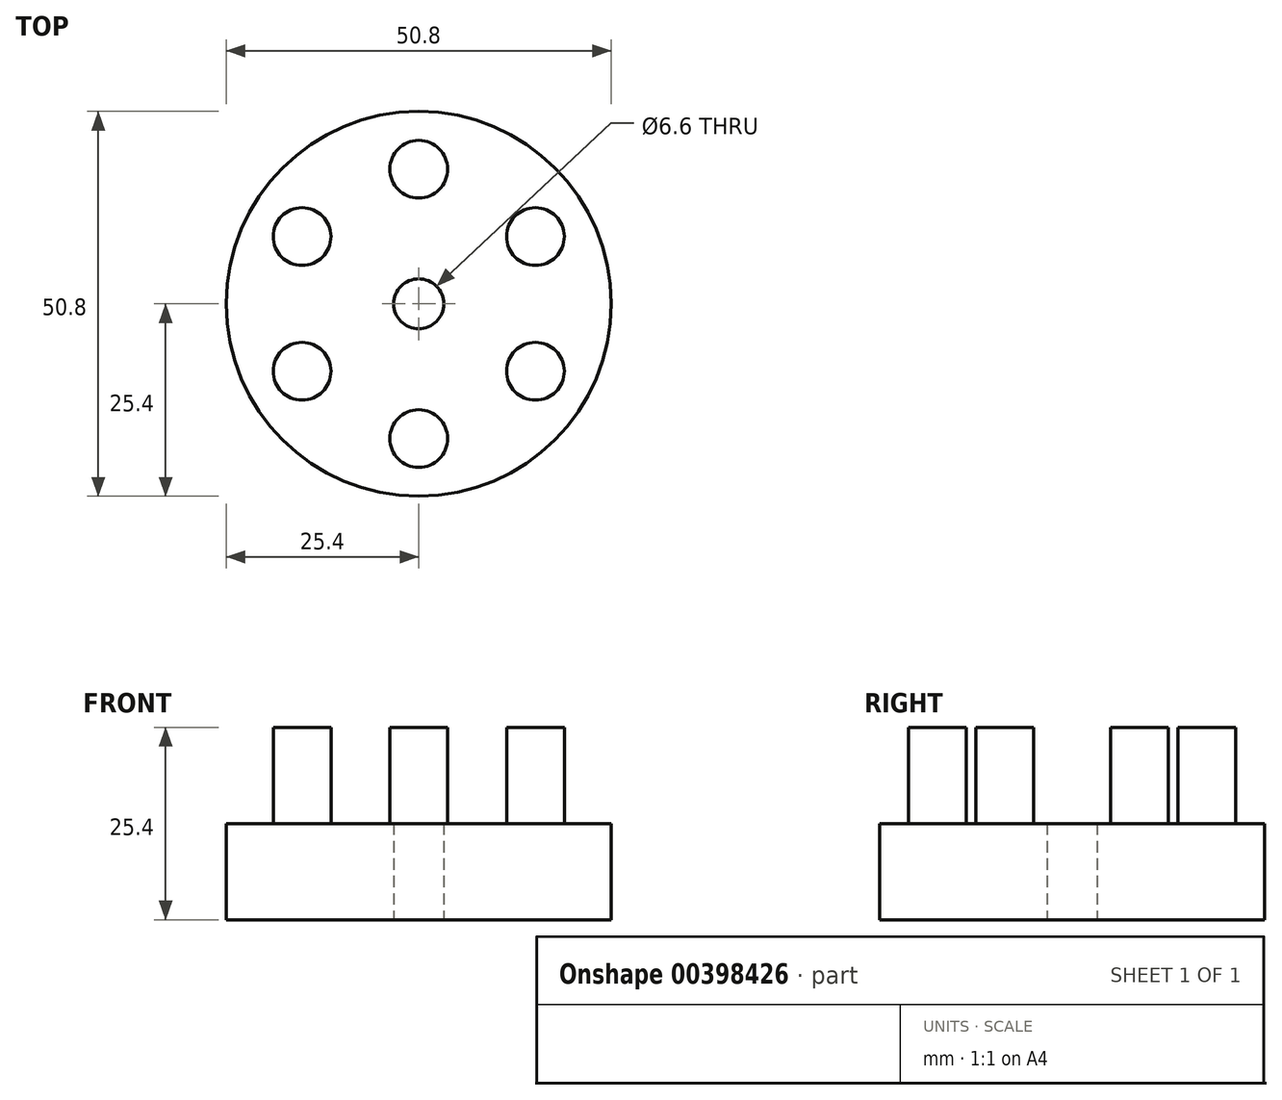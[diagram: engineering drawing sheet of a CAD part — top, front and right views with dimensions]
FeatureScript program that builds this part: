
annotation { "Feature Type Name" : "Feature", "Feature Type Description" : "" }
export const myFeature = defineFeature(function(context is Context, id is Id, definition is map)
    precondition{}
    {
        {
            var Q0;
            Q0=qCreatedBy(makeId("Top.planeOp"),FACE);
            var sketch = newSketch(context, id + "F0", { "sketchPlane" : qUnion([Q0])});
            skCircle(sketch, "E0", {"center": v(0, 0) * mm, "radius": 25.4 * mm});
            skCircle(sketch, "E1", {"center": v(0, 0) * mm, "radius": 3.3 * mm});
            skSolve(sketch);
        }
        {
            var Q0;
            Q0=makeQuery(id+"F0.imprint","IMPRINT",FACE,{"disambiguationData":[TD([[makeQuery(id+"F0.imprint","IMPRINT",EDGE,{"derivedFrom":sQuery(id+"F0.wireOp",EDGE,"E0")}),1.0]])]});
            extrude(context, id + "F1", {"entities" : qUnion([Q0]), "depth" : 12.7 * mm});
        }
        {
            var Q0;
            Q0=makeQuery(id+"F1.opExtrude","CAP_FACE",FACE,{"disambiguationData":[OSD([sQuery(id+"F0.wireOp",EDGE,"E0"),sQuery(id+"F0.wireOp",EDGE,"E1")])],"isStart":false});
            var sketch = newSketch(context, id + "F2", { "sketchPlane" : qUnion([Q0])});
            skLineSegment(sketch, "E2", {"start": v(0, 25.4) * mm, "end": v(0, 17.78) * mm});
            skCircle(sketch, "E3", {"center": v(0, 17.78) * mm, "radius": 3.81 * mm});
            skCircle(sketch, "E4.1.0", {"center": v(-15.4, 8.9) * mm, "radius": 3.81 * mm});
            skCircle(sketch, "E4.2.0", {"center": v(-15.4, -8.89) * mm, "radius": 3.81 * mm});
            skCircle(sketch, "E4.3.0", {"center": v(0, -17.78) * mm, "radius": 3.81 * mm});
            skCircle(sketch, "E4.4.0", {"center": v(15.4, -8.9) * mm, "radius": 3.81 * mm});
            skCircle(sketch, "E4.5.0", {"center": v(15.4, 8.9) * mm, "radius": 3.81 * mm});
            skPoint(sketch, "E4.center", {"position": v(0, 0) * mm});
            skSolve(sketch);
        }
        {
            var Q0;
            Q0 = qSketchRegion(id + "F2", true);
            extrude(context, id + "F3", {"entities" : qUnion([Q0]), "operationType" : NewBodyOperationType.ADD, "depth" : 12.7 * mm});
        }
    });
